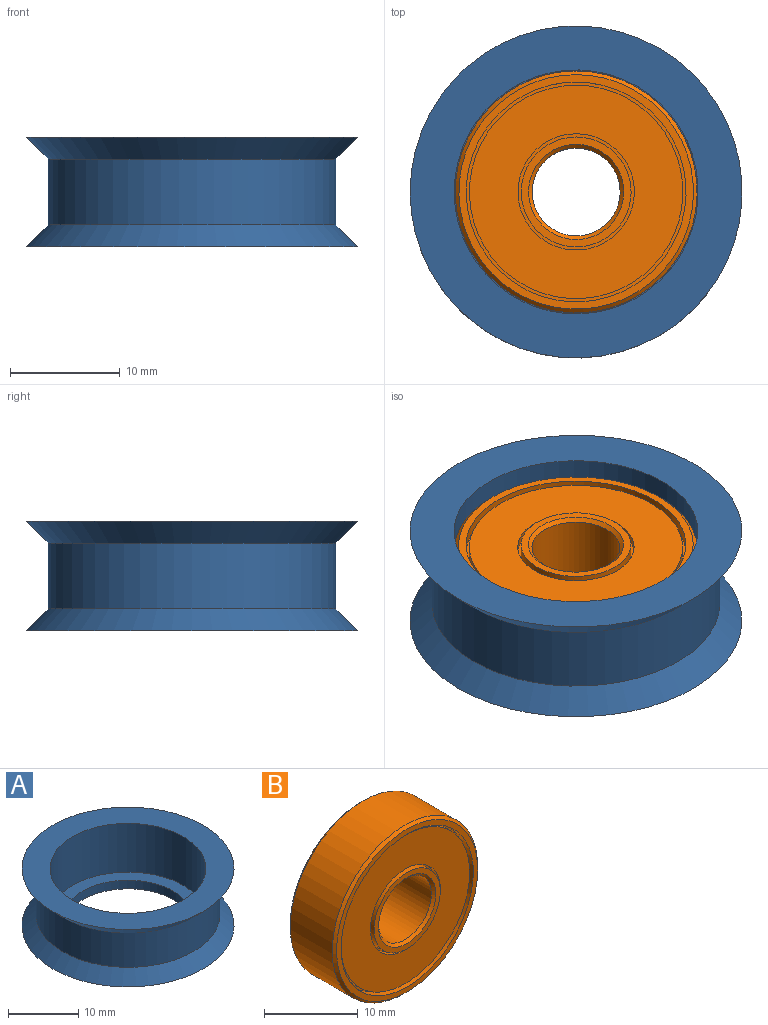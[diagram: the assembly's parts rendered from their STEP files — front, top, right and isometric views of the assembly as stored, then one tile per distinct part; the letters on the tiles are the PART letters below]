
ASSEMBLY  parts=2 mates=1
PART A: 8 faces, bbox 30.2x30.2x10 mm
  f0: plane 30.2x30.2mm, normal (0,0,1), area 329.2mm2, adj f1,f7
  f1: cylinder r=11.1mm len=22.2mm, axis (0,0,-1), area 592.8mm2, adj f0,f2
  f2: plane 22.2x22.2mm, normal (0,0,1), area 126.9mm2, adj f1,f3
  f3: cylinder r=9.1mm len=18.2mm, axis (0,0,-1), area 85.8mm2, adj f2,f4
  f4: plane 30.2x30.2mm, normal (0,0,-1), area 456.2mm2, adj f3,f5
  f5: cone r=13.1mm half-angle=45deg, axis (0,0,-1), area 250.6mm2, adj f4,f6
  f6: cylinder r=13.1mm len=26.2mm, axis (0,0,-1), area 493.9mm2, adj f5,f7
  f7: cone r=15.1mm half-angle=45deg, axis (0,0,1), area 250.6mm2, adj f0,f6
PART B: 32 faces, bbox 22x7x22 mm
  f0: cylinder r=10mm len=20mm, axis (0,1,0), area 62.8mm2, adj f1,f19
  f1: plane 21.34x21.34mm, normal (0,1,0), area 43.5mm2, adj f0,f21
  f2: cylinder r=11mm len=22mm, axis (0,1,0), area 438.2mm2, adj f20,f21
  f3: plane 21.34x21.34mm, normal (0,-1,0), area 43.5mm2, adj f4,f20
  f4: cylinder r=10mm len=20mm, axis (0,1,0), area 62.8mm2, adj f3,f5
  f5: plane 20x20mm, normal (0,-1,0), area 18.1mm2, adj f4,f6
  f6: cylinder r=9.71mm len=19.42mm, axis (0,1,0), area 44.7mm2, adj f5,f7
  f7: plane 19.42x19.42mm, normal (0,-1,0), area 208.1mm2, adj f6,f8
  f8: cylinder r=5.29mm len=10.58mm, axis (0,1,0), area 24.4mm2, adj f7,f9
  f9: plane 10.58x10.58mm, normal (0,-1,0), area 9.4mm2, adj f8,f10
  f10: cylinder r=5mm len=10mm, axis (0,1,0), area 31.4mm2, adj f9,f11
  f11: plane 10x10mm, normal (0,-1,0), area 19.6mm2, adj f10,f22
  f12: cylinder r=4mm len=8mm, axis (0,1,0), area 159.3mm2, adj f22,f23
  f13: plane 10x10mm, normal (0,1,0), area 19.6mm2, adj f14,f23
  f14: cylinder r=5mm len=10mm, axis (0,1,0), area 31.4mm2, adj f13,f15
  f15: plane 10.58x10.58mm, normal (0,1,0), area 9.4mm2, adj f14,f16
  f16: cylinder r=5.29mm len=10.58mm, axis (0,1,0), area 24.4mm2, adj f15,f17
  f17: plane 19.42x19.42mm, normal (0,1,0), area 208.1mm2, adj f16,f18
  f18: cylinder r=9.71mm len=19.42mm, axis (0,1,0), area 44.7mm2, adj f17,f19
  f19: plane 20x20mm, normal (0,1,0), area 18.1mm2, adj f0,f18
  f20: cone r=11mm half-angle=45deg, axis (0,1,0), area 31.8mm2, adj f2,f3
  f21: cone r=10.67mm half-angle=45deg, axis (0,-1,0), area 31.8mm2, adj f1,f2
  f22: cone r=4.33mm half-angle=45deg, axis (0,-1,0), area 12.2mm2, adj f11,f12
  f23: cone r=4mm half-angle=45deg, axis (0,1,0), area 12.2mm2, adj f12,f13
  f24: cylinder r=8.16mm len=16.32mm, axis (0,1,0), area 48.4mm2, adj f25,f31
  f25: torus R=7.5mm, axis (0,1,0), area 219.3mm2, adj f24,f26
  f26: cylinder r=8.16mm len=16.32mm, axis (0,1,0), area 48.4mm2, adj f25,f27
  f27: plane 16.32x16.32mm, normal (0,-1,0), area 62.1mm2, adj f26,f28
  f28: cylinder r=6.84mm len=13.68mm, axis (0,1,0), area 40.6mm2, adj f27,f29
  f29: torus R=7.5mm, axis (0,1,0), area 153.3mm2, adj f28,f30
  f30: cylinder r=6.84mm len=13.68mm, axis (0,1,0), area 40.6mm2, adj f29,f31
  f31: plane 16.32x16.32mm, normal (0,1,0), area 62.1mm2, adj f24,f30
PLACE A t=(0,0,5.2)mm
PLACE B rot(axis=(-1,0,0),90deg) t=(0,0,5)mm
MATE fastened B.f0 <-> A.f1  axis (0,0,-1) through (0,0,1.5)mm
